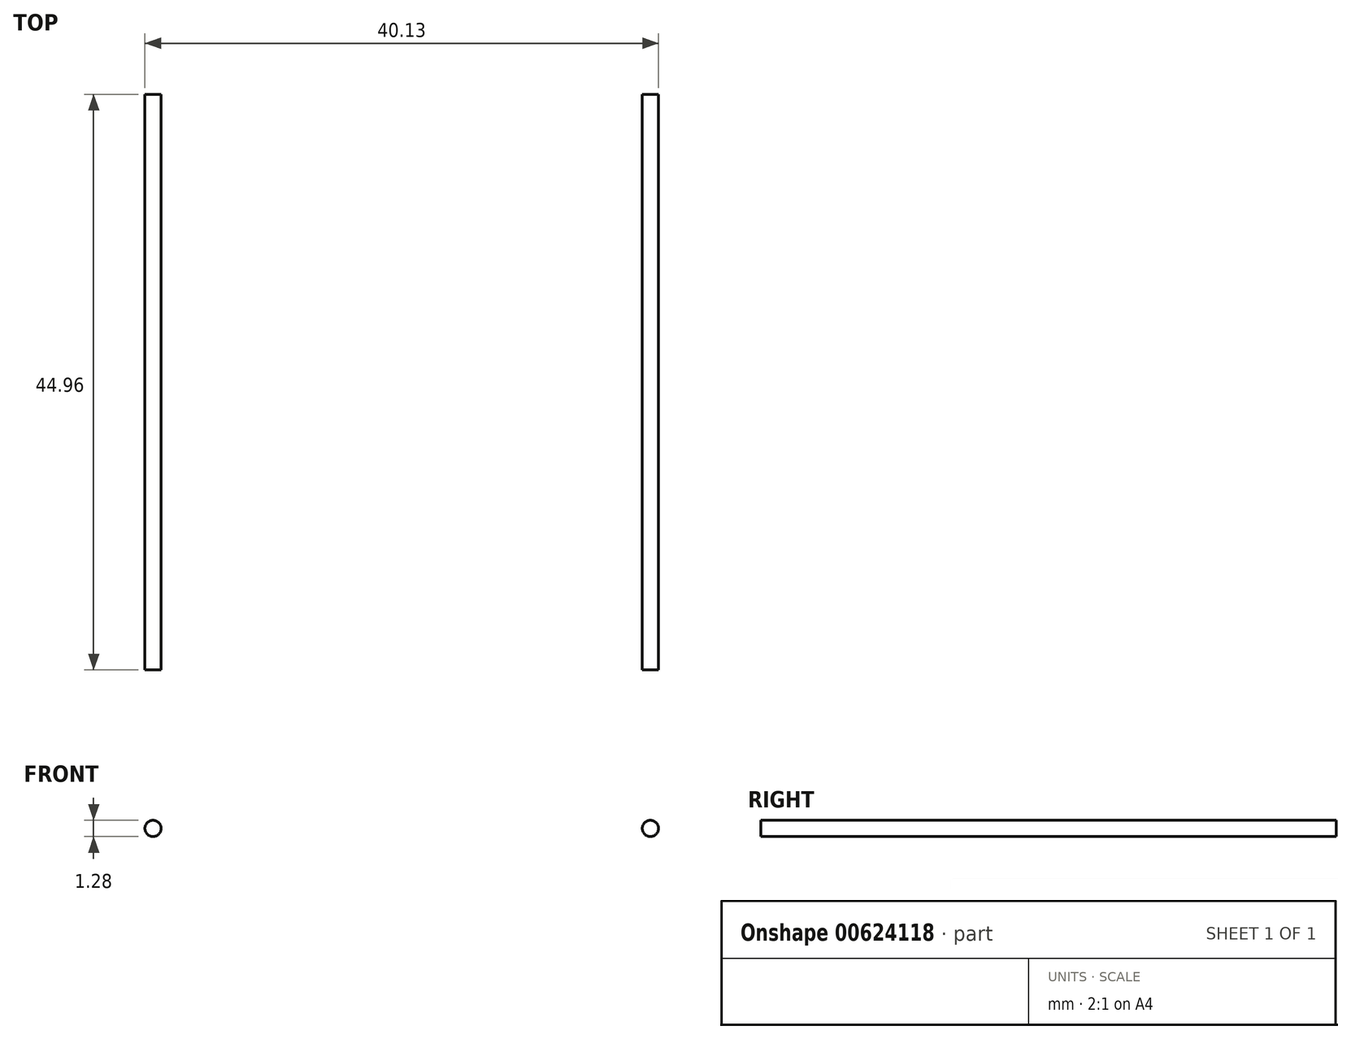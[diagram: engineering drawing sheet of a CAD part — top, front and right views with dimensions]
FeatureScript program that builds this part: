
annotation { "Feature Type Name" : "Feature", "Feature Type Description" : "" }
export const myFeature = defineFeature(function(context is Context, id is Id, definition is map)
    precondition{}
    {
        {
            var Q0;
            Q0=qCreatedBy(makeId("Front.planeOp"),FACE);
            var sketch = newSketch(context, id + "F0", { "sketchPlane" : qUnion([Q0])});
            skCircle(sketch, "E0", {"center": v(-6.53, 0) * mm, "radius": 0.64 * mm});
            skCircle(sketch, "E1", {"center": v(32.33, 0) * mm, "radius": 0.64 * mm});
            skLineSegment(sketch, "E2", {"start": v(13.4, 0) * mm, "end": v(13.4, 8.5) * mm});
            skSolve(sketch);
        }
        {
            var Q0;
            Q0 = qSketchRegion(id + "F0", true);
            extrude(context, id + "F1", {"entities" : qUnion([Q0]), "depth" : 44.96 * mm, "offsetDistance" : 25.4 * mm});
        }
    });
